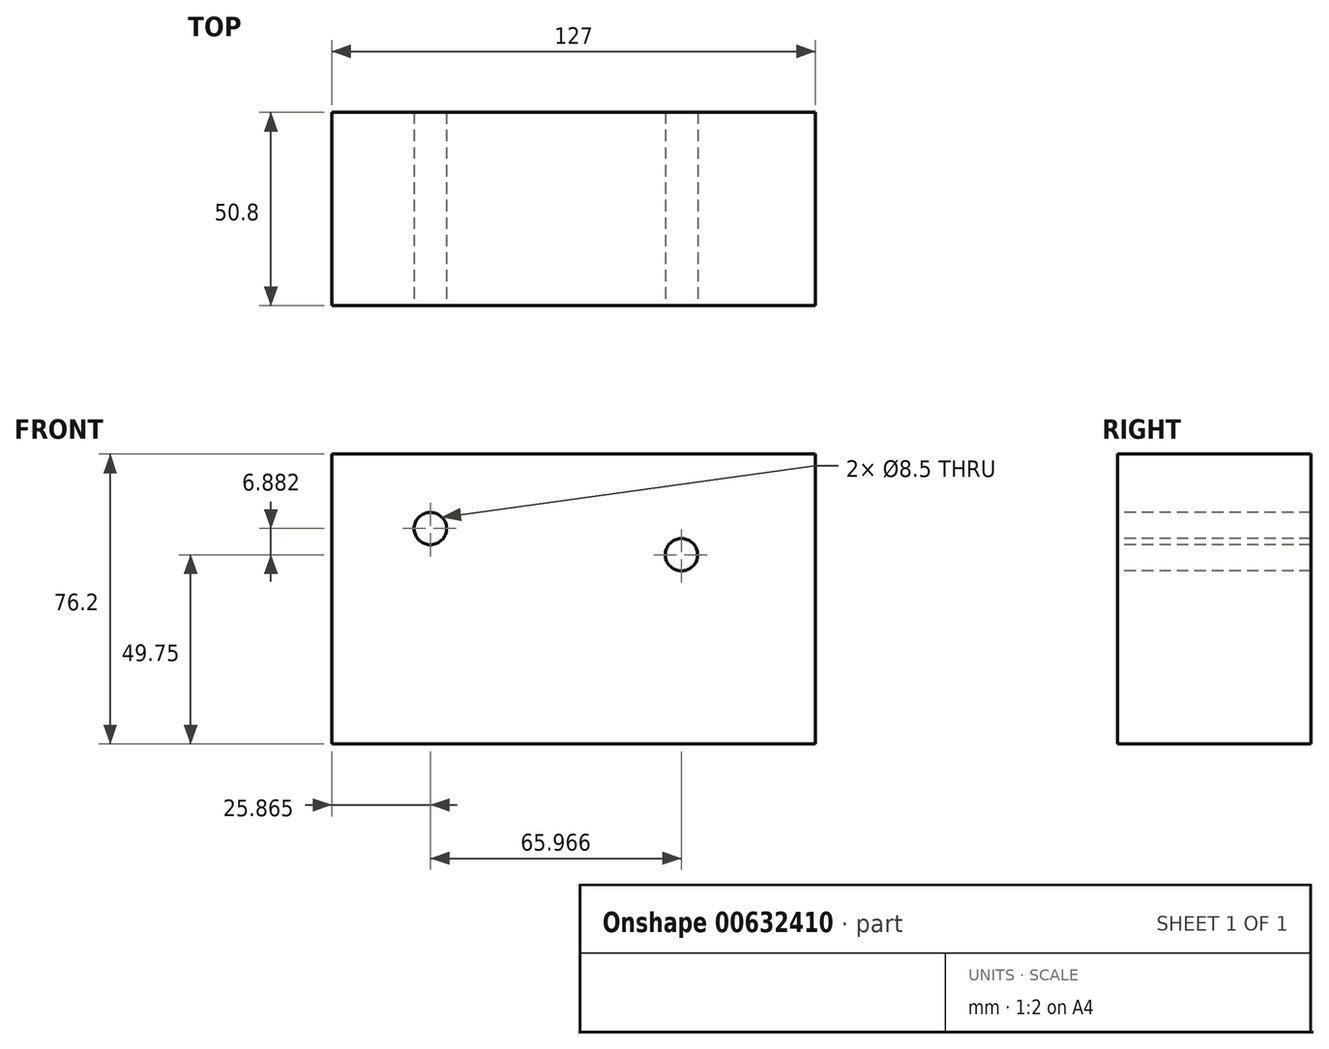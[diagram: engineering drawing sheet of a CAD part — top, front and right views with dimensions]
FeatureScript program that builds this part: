
annotation { "Feature Type Name" : "Feature", "Feature Type Description" : "" }
export const myFeature = defineFeature(function(context is Context, id is Id, definition is map)
    precondition{}
    {
        {
            var Q0;
            Q0=qCreatedBy(makeId("Front.planeOp"),FACE);
            var sketch = newSketch(context, id + "F0", { "sketchPlane" : qUnion([Q0])});
            skLineSegment(sketch, "E0.bottom", {"start": v(-63.5, 38.1) * mm, "end": v(63.5, 38.1) * mm});
            skLineSegment(sketch, "E0.top", {"start": v(-63.5, -38.1) * mm, "end": v(63.5, -38.1) * mm});
            skLineSegment(sketch, "E0.left", {"start": v(-63.5, 38.1) * mm, "end": v(-63.5, -38.1) * mm});
            skLineSegment(sketch, "E0.right", {"start": v(63.5, 38.1) * mm, "end": v(63.5, -38.1) * mm});
            skLineSegment(sketch, "E1", {"start": v(-63.5, -38.1) * mm, "end": v(63.5, 38.1) * mm, "construction": true});
            skSolve(sketch);
        }
        {
            var Q0;
            Q0 = qSketchRegion(id + "F0", true);
            extrude(context, id + "F1", {"entities" : qUnion([Q0]), "depth" : 50.8 * mm, "offsetDistance" : 25.4 * mm});
        }
        {
            var Q0;
            Q0=makeQuery(id+"F1.opExtrude","CAP_FACE",FACE,{"disambiguationData":[OSD([sQuery(id+"F0.wireOp",EDGE,"E0.bottom"),sQuery(id+"F0.wireOp",EDGE,"E0.top"),sQuery(id+"F0.wireOp",EDGE,"E0.left"),sQuery(id+"F0.wireOp",EDGE,"E0.right")])],"isStart":false});
            var sketch = newSketch(context, id + "F2", { "sketchPlane" : qUnion([Q0])});
            skPoint(sketch, "E2", {"position": v(-37.63, 18.53) * mm});
            skPoint(sketch, "E3", {"position": v(28.33, 11.65) * mm});
            skSolve(sketch);
        }
        {
            var Q0;
            Q0=sQuery(id+"F2.wireOp",VERTEX,"E2");
            var Q1;
            Q1=sQuery(id+"F2.wireOp",VERTEX,"E3");
            var Q2;
            Q2=makeQuery(id+"F1.opExtrude","SWEPT_BODY",BODY,{"disambiguationData":[OSD([sQuery(id+"F0.wireOp",EDGE,"E0.bottom"),sQuery(id+"F0.wireOp",EDGE,"E0.top"),sQuery(id+"F0.wireOp",EDGE,"E0.left"),sQuery(id+"F0.wireOp",EDGE,"E0.right")])]});
            hole(context, id + "F3", {"style" : HoleStyle.SIMPLE, "endStyle" : HoleEndStyle.THROUGH, "standardTappedOrClearance" : lookupTablePath({ "standard" : "ISO", "engagement" : "75%", "pitch" : "1.5 mm", "size" : "M10", "type" : "Tapped" }), "standardBlindInLast" : lookupTablePath({ "standard" : "ISO", "engagement" : "75%", "pitch" : "1.5 mm", "size" : "M10", "type" : "Tapped" }), "holeDiameter" : 8.5 * mm, "majorDiameter" : 10 * mm, "showTappedDepth" : true, "isTappedThrough" : true, "tappedDepth" : 12.7 * mm, "tapClearance" : 3, "locations" : qUnion([Q0, Q1]), "scope" : qUnion([Q2])});
        }
    });
